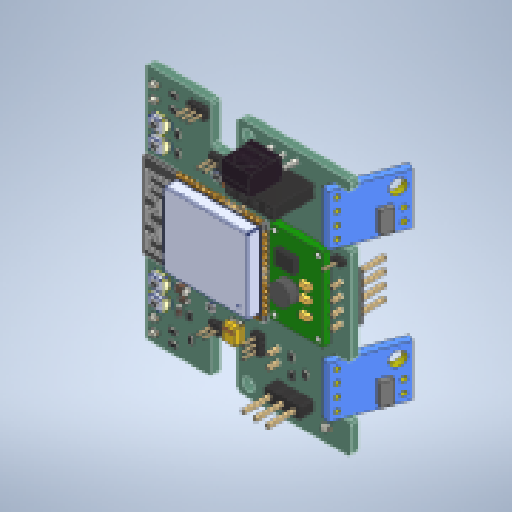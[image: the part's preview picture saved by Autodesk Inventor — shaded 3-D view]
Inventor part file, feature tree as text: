
AUTODESK INVENTOR PART (.ipt)
format: ipt  version: 2023.5 (Build 275446000, 446)  size: 2,994,688 bytes
history: native  units: mm
features: other x126, extrude x1, sketch x1, projected_geometry x1
ambient origin geometry x8: Origin, YZ Plane, XZ Plane, XY Plane, X Axis, Y Axis, Z Axis, Center Point
bodies: Body1 (feature_tree), Body2 (feature_tree), Body3 (feature_tree), Body4 (feature_tree), Body5 (feature_tree), Body6 (feature_tree), Body7 (feature_tree), Body8 (feature_tree), Body9 (feature_tree), Body10 (feature_tree), Body11 (feature_tree), Body12 (feature_tree), Body13 (feature_tree), Body14 (feature_tree), Body15 (feature_tree), Body16 (feature_tree), Body17 (feature_tree), Body18 (feature_tree), Body19 (feature_tree), Body20 (feature_tree), Body21 (feature_tree), Body22 (feature_tree), Body23 (feature_tree), Body24 (feature_tree), Body25 (feature_tree), Body26 (feature_tree), Body27 (feature_tree), Body28 (feature_tree), Body29 (feature_tree), Body30 (feature_tree), Body31 (feature_tree), Body32 (feature_tree), Body33 (feature_tree), Body34 (feature_tree), Body35 (feature_tree), Body36 (feature_tree), Body37 (feature_tree), Body38 (feature_tree), Body39 (feature_tree), Body40 (feature_tree), Body41 (feature_tree), Body42 (feature_tree), Body43 (feature_tree), Body44 (feature_tree), Body45 (feature_tree), Body46 (feature_tree), Body47 (feature_tree), Body48 (feature_tree), Body49 (feature_tree), Body50 (feature_tree), Body51 (feature_tree), Body52 (feature_tree), Body53 (feature_tree), Body54 (feature_tree), Body55 (feature_tree), Body56 (feature_tree), Body57 (feature_tree), Body58 (feature_tree), Body59 (feature_tree), Body60 (feature_tree), Body61 (feature_tree), Body62 (feature_tree), Body63 (feature_tree), Body64 (feature_tree), Body65 (feature_tree), Body66 (feature_tree), Body67 (feature_tree), Body68 (feature_tree), Body69 (feature_tree), Body70 (feature_tree), Body71 (feature_tree), Body72 (feature_tree), Body73 (feature_tree), Body74 (feature_tree), Body75 (feature_tree), Body76 (feature_tree), Body77 (feature_tree), Body78 (feature_tree), Body79 (feature_tree), Body80 (feature_tree), Body81 (feature_tree), Body82 (feature_tree), Body83 (feature_tree), Body84 (feature_tree), Body85 (feature_tree), Body86 (feature_tree), Body87 (feature_tree), Body88 (feature_tree), Body89 (feature_tree), Body90 (feature_tree), Body91 (feature_tree), Body92 (feature_tree), Body93 (feature_tree), Body94 (feature_tree), Body95 (feature_tree), Body96 (feature_tree), Body97 (feature_tree), Body98 (feature_tree), Body99 (feature_tree), Body100 (feature_tree), Body101 (feature_tree), Body102 (feature_tree), Body103 (feature_tree), Body104 (feature_tree), Body105 (feature_tree), Body106 (feature_tree), Body107 (feature_tree), Body108 (feature_tree), Body109 (feature_tree), Body110 (feature_tree), Body111 (feature_tree), Body112 (feature_tree), Body113 (feature_tree), Body114 (feature_tree), Body115 (feature_tree), Body116 (feature_tree), Body117 (feature_tree), Body118 (feature_tree), Body119 (feature_tree), Body120 (feature_tree), Body121 (feature_tree), Body122 (feature_tree), Body123 (feature_tree), Body124 (feature_tree), Body125 (feature_tree), Body126 (feature_tree)
feature tree (129):
  other  "Bryła1"
  extrude  "Wyciągnięcie proste1"  Depth=1.1mm TaperAngle=0.0deg
  other  "Bryła2"
  other  "Bryła3"
  other  "Bryła4"
  other  "Bryła5"
  other  "Bryła6"
  other  "Bryła7"
  other  "Bryła8"
  other  "Bryła9"
  other  "Bryła10"
  other  "Bryła11"
  other  "Bryła12"
  other  "Bryła13"
  other  "Bryła14"
  other  "Bryła15"
  other  "Bryła16"
  other  "Bryła17"
  other  "Bryła18"
  other  "Bryła19"
  other  "Bryła20"
  other  "Bryła21"
  other  "Bryła22"
  other  "Bryła23"
  other  "Bryła24"
  other  "Bryła25"
  other  "Bryła26"
  other  "Bryła27"
  other  "Bryła28"
  other  "Bryła29"
  other  "Bryła30"
  other  "Bryła31"
  other  "Bryła32"
  other  "Bryła33"
  other  "Bryła34"
  other  "Bryła35"
  other  "Bryła36"
  other  "Bryła37"
  other  "Bryła38"
  other  "Bryła39"
  other  "Bryła40"
  other  "Bryła41"
  other  "Bryła42"
  other  "Bryła43"
  other  "Bryła44"
  other  "Bryła45"
  other  "Bryła46"
  other  "Bryła47"
  other  "Bryła48"
  other  "Bryła49"
  other  "Bryła50"
  other  "Bryła51"
  other  "Bryła52"
  other  "Bryła53"
  other  "Bryła54"
  other  "Bryła55"
  other  "Bryła56"
  other  "Bryła57"
  other  "Bryła58"
  other  "Bryła59"
  other  "Bryła60"
  other  "Bryła61"
  other  "Bryła62"
  other  "Bryła63"
  other  "Bryła64"
  other  "Bryła65"
  other  "Bryła66"
  other  "Bryła67"
  other  "Bryła68"
  other  "Bryła69"
  other  "Bryła70"
  other  "Bryła71"
  other  "Bryła72"
  other  "Bryła73"
  other  "Bryła74"
  other  "Bryła75"
  other  "Bryła76"
  other  "Bryła77"
  other  "Bryła78"
  other  "Bryła79"
  other  "Bryła80"
  other  "Bryła81"
  other  "Bryła82"
  other  "Bryła83"
  other  "Bryła84"
  other  "Bryła85"
  other  "Bryła86"
  other  "Bryła87"
  other  "Bryła88"
  other  "Bryła89"
  other  "Bryła90"
  other  "Bryła91"
  other  "Bryła92"
  other  "Bryła93"
  other  "Bryła94"
  other  "Bryła95"
  other  "Bryła96"
  other  "Bryła97"
  other  "Bryła98"
  other  "Bryła99"
  other  "Bryła100"
  other  "Bryła101"
  other  "Bryła102"
  other  "Bryła103"
  other  "Bryła104"
  other  "Bryła105"
  other  "Bryła106"
  other  "Bryła107"
  other  "Bryła108"
  other  "Bryła109"
  other  "Bryła110"
  other  "Bryła111"
  other  "Bryła112"
  other  "Bryła113"
  other  "Bryła114"
  other  "Bryła115"
  other  "Bryła116"
  other  "Bryła117"
  other  "Bryła118"
  other  "Bryła119"
  other  "Bryła120"
  other  "Bryła121"
  other  "Bryła122"
  other  "Bryła123"
  other  "Bryła124"
  other  "Bryła125"
  other  "Bryła126"
  sketch  "Szkic1"
  projected_geometry  "Pętla rzutowana1"
